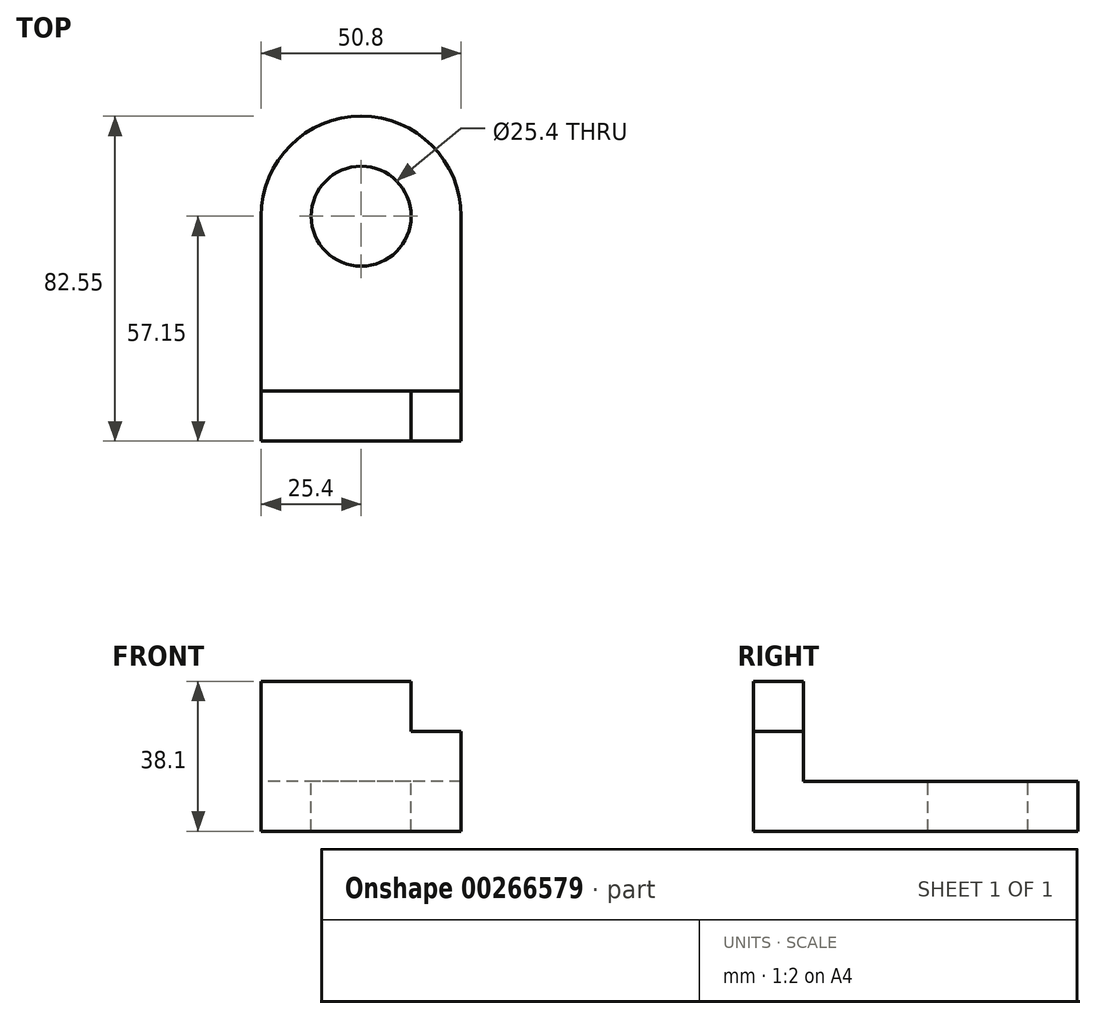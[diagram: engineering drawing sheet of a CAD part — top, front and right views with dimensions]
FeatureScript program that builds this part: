
annotation { "Feature Type Name" : "Feature", "Feature Type Description" : "" }
export const myFeature = defineFeature(function(context is Context, id is Id, definition is map)
    precondition{}
    {
        {
            var Q0;
            Q0=qCreatedBy(makeId("Front.planeOp"),FACE);
            var sketch = newSketch(context, id + "F0", { "sketchPlane" : qUnion([Q0])});
            skLineSegment(sketch, "E0.bottom", {"start": v(25.4, -19.05) * mm, "end": v(-25.4, -19.05) * mm});
            skLineSegment(sketch, "E0.top", {"start": v(25.4, 19.05) * mm, "end": v(-25.4, 19.05) * mm});
            skLineSegment(sketch, "E0.left", {"start": v(25.4, -19.05) * mm, "end": v(25.4, 19.05) * mm});
            skLineSegment(sketch, "E0.right", {"start": v(-25.4, -19.05) * mm, "end": v(-25.4, 19.05) * mm});
            skPoint(sketch, "E0.middle", {"position": v(0, 0) * mm});
            skSolve(sketch);
        }
        {
            var Q0;
            Q0=makeQuery(id+"F0.imprint","IMPRINT",FACE,{"disambiguationData":[TD([[makeQuery(id+"F0.imprint","IMPRINT",EDGE,{"derivedFrom":sQuery(id+"F0.wireOp",EDGE,"E0.bottom")}),-1.0]])]});
            extrude(context, id + "F1", {"entities" : qUnion([Q0]), "depth" : 12.7 * mm});
        }
        {
            var Q0;
            Q0=qCreatedBy(makeId("Front.planeOp"),FACE);
            var sketch = newSketch(context, id + "F2", { "sketchPlane" : qUnion([Q0])});
            skLineSegment(sketch, "E1.bottom", {"start": v(29.8, 22.31) * mm, "end": v(12.7, 22.31) * mm});
            skLineSegment(sketch, "E1.top", {"start": v(29.8, 6.35) * mm, "end": v(12.7, 6.35) * mm});
            skLineSegment(sketch, "E1.left", {"start": v(29.8, 22.31) * mm, "end": v(29.8, 6.35) * mm});
            skLineSegment(sketch, "E1.right", {"start": v(12.7, 22.31) * mm, "end": v(12.7, 6.35) * mm});
            skSolve(sketch);
        }
        {
            var Q0;
            Q0 = qSketchRegion(id + "F2", true);
            extrude(context, id + "F3", {"entities" : qUnion([Q0]), "operationType" : NewBodyOperationType.REMOVE, "endBound" : BoundingType.THROUGH_ALL, "depth" : 25.4 * mm});
        }
        {
            var Q0;
            Q0=makeQuery(id+"F1.opExtrude","SWEPT_FACE",FACE,{"disambiguationData":[OSD([sQuery(id+"F0.wireOp",EDGE,"E0.bottom")])]});
            var sketch = newSketch(context, id + "F4", { "sketchPlane" : qUnion([Q0])});
            skLineSegment(sketch, "E2.bottom", {"start": v(25.4, 0) * mm, "end": v(-25.4, 0) * mm});
            skLineSegment(sketch, "E2.top", {"start": v(25.4, -44.45) * mm, "end": v(-25.4, -44.45) * mm});
            skLineSegment(sketch, "E2.left", {"start": v(25.4, 0) * mm, "end": v(25.4, -44.45) * mm});
            skLineSegment(sketch, "E2.right", {"start": v(-25.4, 0) * mm, "end": v(-25.4, -44.45) * mm});
            skSolve(sketch);
        }
        {
            var Q0;
            Q0=makeQuery(id+"F4.imprint","IMPRINT",FACE,{"disambiguationData":[TD([[makeQuery(id+"F4.imprint","IMPRINT",EDGE,{"derivedFrom":sQuery(id+"F4.wireOp",EDGE,"E2.bottom")}),1.0]])]});
            extrude(context, id + "F5", {"entities" : qUnion([Q0]), "operationType" : NewBodyOperationType.ADD, "oppositeDirection" : true, "depth" : 12.7 * mm});
        }
        {
            var Q0;
            Q0=makeQuery(id+"F5.opExtrude","CAP_FACE",FACE,{"disambiguationData":[OSD([sQuery(id+"F4.wireOp",EDGE,"E2.bottom"),sQuery(id+"F4.wireOp",EDGE,"E2.top"),sQuery(id+"F4.wireOp",EDGE,"E2.left"),sQuery(id+"F4.wireOp",EDGE,"E2.right")])],"isStart":false});
            var sketch = newSketch(context, id + "F6", { "sketchPlane" : qUnion([Q0])});
            skArc(sketch, "E3", {"start": v(25.4, 44.45) * mm, "mid": v(0, 69.85) * mm, "end": v(-25.4, 44.45) * mm});
            skSolve(sketch);
        }
        {
            var Q0;
            Q0 = qSketchRegion(id + "F6", true);
            var Q1;
            Q1=makeQuery(id+"F6.imprint","IMPRINT",FACE,{"disambiguationData":[TD([[makeQuery(id+"F6.imprint","IMPRINT",EDGE,{"derivedFrom":sQuery(id+"F6.wireOp",EDGE,"E3")}),1.0]])]});
            extrude(context, id + "F7", {"entities" : qUnion([Q0, Q1]), "operationType" : NewBodyOperationType.ADD, "oppositeDirection" : true, "depth" : 12.7 * mm});
        }
        {
            var Q0;
            {var subQ0=sQuery(id+"F4.wireOp",EDGE,"E2.top");Q0=makeQuery(id+"F7.boolean.opBoolean","MERGE",FACE,{"derivedFrom":[makeQuery(id+"F5.opExtrude","CAP_FACE",FACE,{"disambiguationData":[OSD([sQuery(id+"F4.wireOp",EDGE,"E2.bottom"),subQ0,sQuery(id+"F4.wireOp",EDGE,"E2.left"),sQuery(id+"F4.wireOp",EDGE,"E2.right")])],"isStart":false}),makeQuery(id+"F7.opExtrude","CAP_FACE",FACE,{"disambiguationData":[OSD([subQ0,sQuery(id+"F6.wireOp",EDGE,"E3")])],"isStart":true})]});}
            var sketch = newSketch(context, id + "F8", { "sketchPlane" : qUnion([Q0])});
            skCircle(sketch, "E4", {"center": v(0, 44.45) * mm, "radius": 12.7 * mm});
            skSolve(sketch);
        }
        {
            var Q0;
            Q0 = qSketchRegion(id + "F8", true);
            extrude(context, id + "F9", {"entities" : qUnion([Q0]), "operationType" : NewBodyOperationType.REMOVE, "endBound" : BoundingType.THROUGH_ALL, "oppositeDirection" : true, "depth" : 25.4 * mm});
        }
    });
